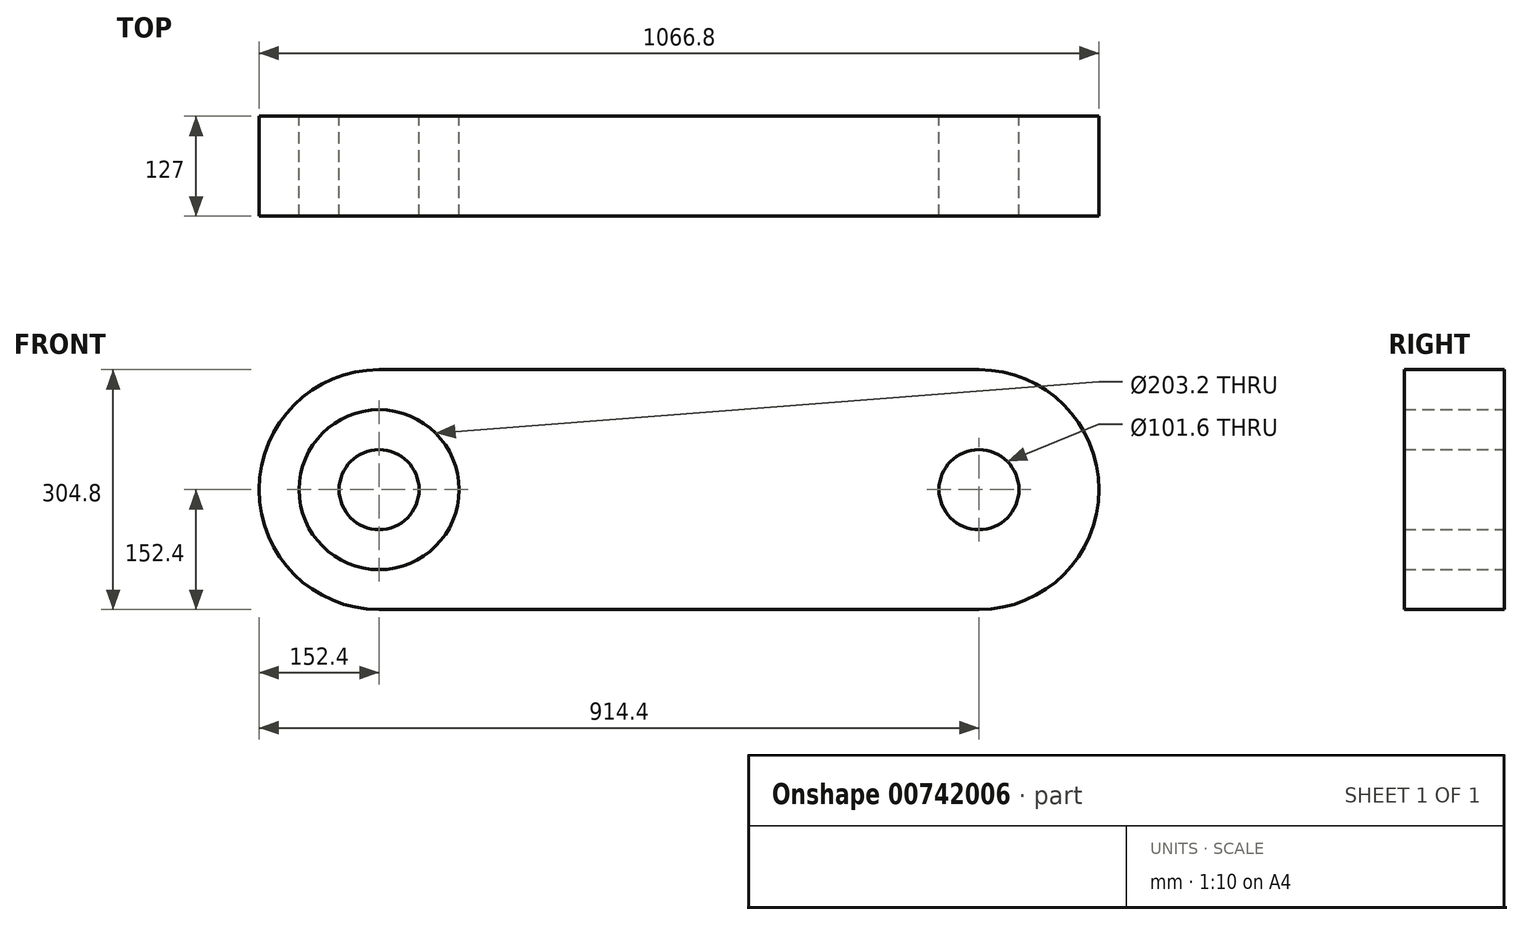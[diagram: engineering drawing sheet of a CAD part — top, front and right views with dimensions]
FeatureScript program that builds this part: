
annotation { "Feature Type Name" : "Feature", "Feature Type Description" : "" }
export const myFeature = defineFeature(function(context is Context, id is Id, definition is map)
    precondition{}
    {
        {
            var Q0;
            Q0=qCreatedBy(makeId("Front.planeOp"),FACE);
            var sketch = newSketch(context, id + "F0", { "sketchPlane" : qUnion([Q0])});
            skCircle(sketch, "E0", {"center": v(-381, 0) * mm, "radius": 50.8 * mm});
            skCircle(sketch, "E1", {"center": v(-381, 0) * mm, "radius": 101.6 * mm});
            skCircle(sketch, "E2", {"center": v(-381, 0) * mm, "radius": 152.4 * mm});
            skLineSegment(sketch, "E3", {"start": v(-381, 152.4) * mm, "end": v(0, 152.4) * mm});
            skLineSegment(sketch, "E4", {"start": v(-381, -152.4) * mm, "end": v(0, -152.4) * mm});
            skCircle(sketch, "E5.MirrorC", {"center": v(381, 0) * mm, "radius": 152.4 * mm});
            skLineSegment(sketch, "E6.MirrorCS", {"start": v(381, 152.4) * mm, "end": v(0, 152.4) * mm});
            skLineSegment(sketch, "E7.MirrorCS", {"start": v(381, -152.4) * mm, "end": v(0, -152.4) * mm});
            skCircle(sketch, "E8.MirrorC", {"center": v(381, 0) * mm, "radius": 101.6 * mm});
            skCircle(sketch, "E9.MirrorC", {"center": v(381, 0) * mm, "radius": 50.8 * mm});
            skSolve(sketch);
        }
        {
            var Q0;
            Q0 = qSketchRegion(id + "F0", true);
            var Q1;
            Q1=makeQuery(id+"F0.imprint","IMPRINT",FACE,{"disambiguationData":[TD([[makeQuery(id+"F0.imprint","IMPRINT",EDGE,{"derivedFrom":sQuery(id+"F0.wireOp",EDGE,"E0")}),1.0]])]});
            var Q2;
            Q2=makeQuery(id+"F0.imprint","IMPRINT",FACE,{"disambiguationData":[TD([[makeQuery(id+"F0.imprint","IMPRINT",EDGE,{"derivedFrom":sQuery(id+"F0.wireOp",EDGE,"E9.MirrorC")}),-1.0]])]});
            extrude(context, id + "F1", {"entities" : qUnion([Q0, Q1, Q2]), "endBound" : BoundingType.SYMMETRIC, "depth" : 127 * mm, "offsetDistance" : 25.4 * mm});
        }
    });
